FCSTD DOCUMENT  (FreeCAD 0.19R)
Label: Board Outline
License: All rights reserved
LicenseURL: http://en.wikipedia.org/wiki/All_rights_reserved
objects: Sketcher::SketchObject×1, PartDesign::Body×1
note: 2 computed .brp shape members not serialized (recipe doc carries the construction recipe); baked Part::Feature solids carry a one-line shape summary decoded from their .brp

FEATURE [Sketcher::SketchObject] Sketch
  FullyConstrained = true
  MapMode = 5
  Support = -> [XY_Plane]
  sketch-geometry (25):
    g0: LineSegment StartX=0 StartY=0.8 StartZ=0 EndX=0 EndY=25.85 EndZ=0
    g1: LineSegment StartX=-1.41261 StartY=28.8536 StartZ=0 EndX=-2 EndY=31.4376 EndZ=0
    g2: LineSegment StartX=-1.39722 StartY=32.3951 StartZ=0 EndX=11.1624 EndY=35.25 EndZ=0
    g3: LineSegment StartX=12.1198 StartY=34.6472 StartZ=0 EndX=13.35 EndY=29.2353 EndZ=0
    g4: LineSegment StartX=13.35 StartY=29.2353 StartZ=0 EndX=13.35 EndY=13.8 EndZ=0
    g5: LineSegment StartX=14.15 StartY=13 StartZ=0 EndX=22.7 EndY=13 EndZ=0
    g6: LineSegment StartX=23.5 StartY=12.2 StartZ=0 EndX=23.5 EndY=0.8 EndZ=0
    g7: LineSegment StartX=22.7 StartY=0 StartZ=0 EndX=0.8 EndY=0 EndZ=0
    g8: ArcOfCircle CenterX=14.15 CenterY=13.8 CenterZ=0 NormalX=0 NormalY=0 NormalZ=1 AngleXU=0 Radius=0.8 StartAngle=3.14159 EndAngle=4.71239
    g9: ArcOfCircle CenterX=22.7 CenterY=12.2 CenterZ=0 NormalX=0 NormalY=0 NormalZ=1 AngleXU=0 Radius=0.8 StartAngle=7e-16 EndAngle=1.5708
    g10: ArcOfCircle CenterX=22.7 CenterY=0.8 CenterZ=0 NormalX=0 NormalY=0 NormalZ=1 AngleXU=0 Radius=0.8 StartAngle=4.71239 EndAngle=6.28319
    g11: ArcOfCircle CenterX=-1.2199 CenterY=31.615 CenterZ=0 NormalX=0 NormalY=0 NormalZ=1 AngleXU=0 Radius=0.8 StartAngle=1.79431 EndAngle=3.36511
    g12: ArcOfCircle CenterX=0.8 CenterY=0.8 CenterZ=0 NormalX=0 NormalY=0 NormalZ=1 AngleXU=0 Radius=0.8 StartAngle=3.14159 EndAngle=4.71239
    g13: ArcOfCircle CenterX=11.3397 CenterY=34.4699 CenterZ=0 NormalX=0 NormalY=0 NormalZ=1 AngleXU=0 Radius=0.8 StartAngle=0.223513 EndAngle=1.79431
    g14: LineSegment StartX=-1.41261 StartY=28.8536 StartZ=0 EndX=0 EndY=25.85 EndZ=0
    g15: LineSegment StartX=13.35 StartY=29.2353 StartZ=0 EndX=11.9425 EndY=35.4273 EndZ=0
    g16: LineSegment StartX=11.9425 StartY=35.4273 StartZ=0 EndX=11.1624 EndY=35.25 EndZ=0
    g17: Circle CenterX=2.7 CenterY=12.7762 CenterZ=0 NormalX=0 NormalY=0 NormalZ=1 AngleXU=0 Radius=1.1
    g18: Circle CenterX=20.35 CenterY=9.4 CenterZ=0 NormalX=0 NormalY=0 NormalZ=1 AngleXU=0 Radius=1.1
    g19: LineSegment StartX=-2.16059 StartY=35.1443 StartZ=0 EndX=10.6623 EndY=38.059 EndZ=0
    g20: LineSegment StartX=10.6623 StartY=38.059 StartZ=0 EndX=13.5438 EndY=25.3824 EndZ=0
    g21: LineSegment StartX=13.5438 StartY=25.3824 StartZ=0 EndX=0.720943 EndY=22.4676 EndZ=0
    g22: LineSegment StartX=0.720943 StartY=22.4676 StartZ=0 EndX=-2.16059 EndY=35.1443 EndZ=0
    g23: LineSegment StartX=-1.39722 StartY=32.3951 StartZ=0 EndX=-1.52887 EndY=32.3651 EndZ=0
    g24: LineSegment StartX=11.1624 StartY=35.25 StartZ=0 EndX=11.294 EndY=35.2799 EndZ=0
  constraints (68):
    c: Coincident(g3,g4)
    c: Horizontal(g5)
    c: Vertical(g6)
    c: Parallel(g4,g0)
    c: Tangent(g4,g8) = -1.5708
    c: Tangent(g5,g8) = -1.5708
    c: Tangent(g5,g9) = 1.5708
    c: Tangent(g6,g9) = 1.5708
    c: Tangent(g6,g10) = 1.5708
    c: Tangent(g7,g10) = 1.5708
    c: Tangent(g1,g11) = 1.5708
    c: Tangent(g2,g11) = 1.5708
    c: Tangent(g0,g12) = 1.5708
    c: Tangent(g7,g12) = 1.5708
    c: Tangent(g2,g13) = 1.5708
    c: Tangent(g3,g13) = 1.5708
    c: Equal(g11,g13)
    c: Equal(g13,g8)
    c: Equal(g8,g9)
    c: Equal(g9,g10)
    c: Equal(g10,g12)
    c: Horizontal(g7)
    c: Vertical(g0)
    c: PointOnObject(g7,g-1)
    c: PointOnObject(g0,g-2)
    c: Coincident(g14,g1)
    c: Coincident(g14,g0)
    c: Parallel(g1,g3)
    c: Radius(g9) = 0.8
    c: Distance(g3,g1) = 14.48
    c: DistanceX(g0,g6) = 23.5
    c: DistanceY(g7,g5) = 13
    c: DistanceX(g0,g4) = 13.35
    c: DistanceY(g7,g2) = 35.25
    c: DistanceX(g1,g6) = 25.5
    c: Coincident(g15,g3)
    c: Tangent(g15,g13)
    c: Coincident(g16,g15)
    c: Coincident(g16,g2)
    c: Perpendicular(g15,g16)
    c: Parallel(g2,g16)
    c: Distance(g15) = 6.35
    c: Distance(g1) = 2.65
    c: DistanceY(g7,g0) = 25.85
    c: Equal(g17,g18)
    c: Radius(g18) = 1.1
    c: DistanceY(g18,g5) = 3.6
    c: DistanceX(g18,g6) = 3.15
    c: DistanceX(g0,g17) = 2.7
    c: Distance(g17,g18) = 17.97
    c: Coincident(g19,g20)
    c: Coincident(g20,g21)
    c: Coincident(g21,g22)
    c: Coincident(g22,g19)
    c: Parallel(g22,g20)
    c: Parallel(g19,g21)
    c: Angle(g19,g20) = 1.5708
    c: Distance(g20) = 13
    c: Distance(g19) = 13.15
    c: Parallel(g19,g2)
    c: Coincident(g23,g2)
    c: PointOnObject(g23,g22)
    c: Perpendicular(g22,g23)
    c: Coincident(g24,g2)
    c: PointOnObject(g24,g20)
    c: Perpendicular(g20,g24)
    c: Equal(g24,g23)
    c: Distance(g24,g19) = 2.85
FEATURE [PartDesign::Body] Body
  Group = -> [Sketch]
  Origin = -> Origin
